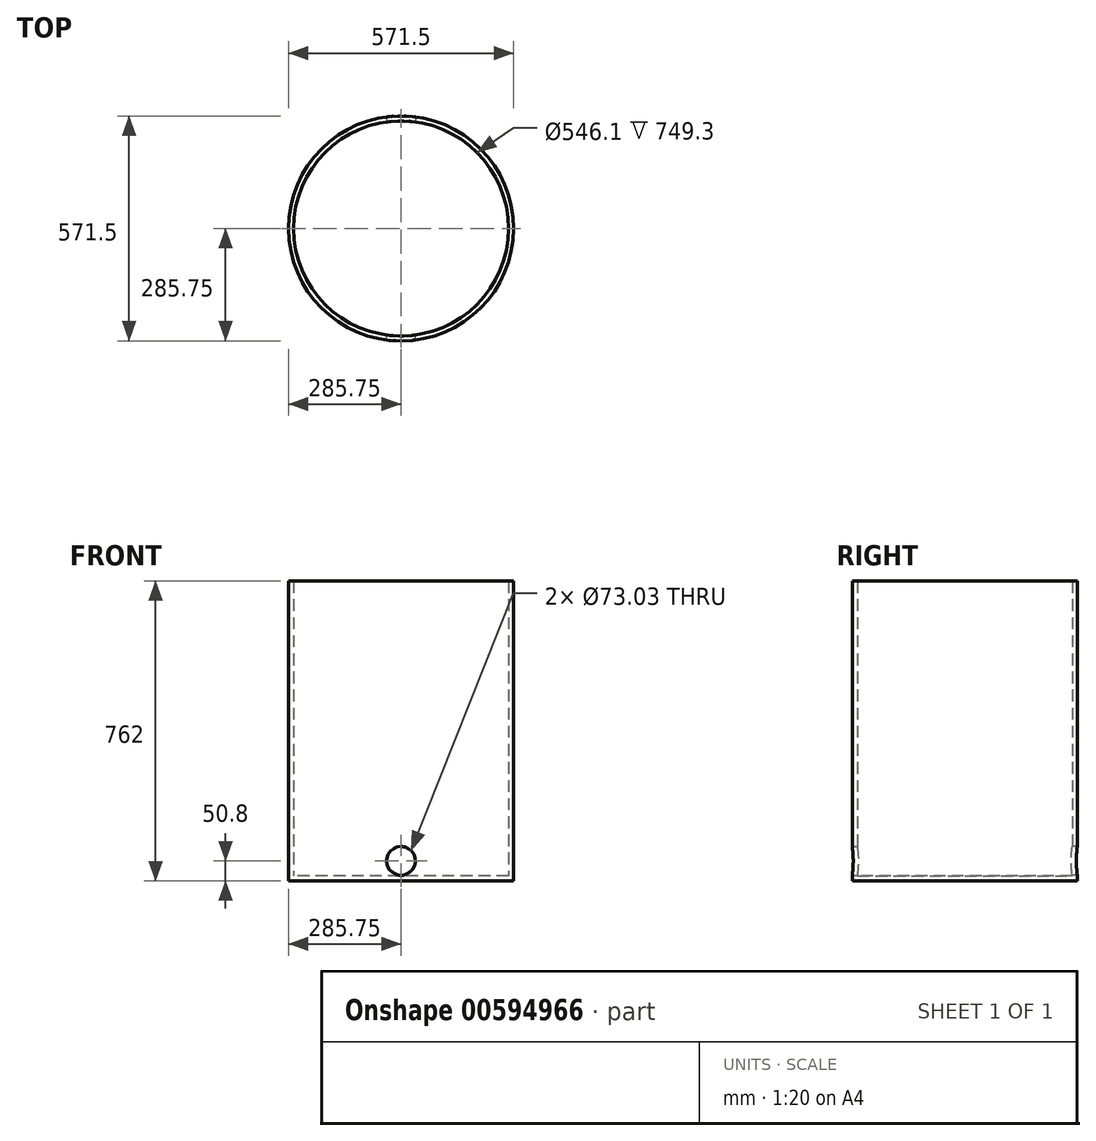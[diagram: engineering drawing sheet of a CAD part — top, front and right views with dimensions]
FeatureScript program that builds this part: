
annotation { "Feature Type Name" : "Feature", "Feature Type Description" : "" }
export const myFeature = defineFeature(function(context is Context, id is Id, definition is map)
    precondition{}
    {
        {
            var Q0;
            Q0=qCreatedBy(makeId("Top.planeOp"),FACE);
            var sketch = newSketch(context, id + "F0", { "sketchPlane" : qUnion([Q0])});
            skCircle(sketch, "E0", {"center": v(0, 0) * mm, "radius": 285.75 * mm});
            skSolve(sketch);
        }
        {
            var Q0;
            Q0=qSketchRegion(id+"F0",true);
            extrude(context, id + "F1", {"entities" : qUnion([Q0]), "depth" : 762 * mm, "offsetDistance" : 25.4 * mm});
        }
        {
            var Q0;
            Q0=makeQuery(id+"F1.opExtrude","CAP_FACE",FACE,{"disambiguationData":[OSD([sQuery(id+"F0.wireOp",EDGE,"E0")])],"isStart":false});
            shell(context, id + "F2", {"entities" : qUnion([Q0]), "thickness" : 12.7 * mm});
        }
        {
            var Q0;
            Q0=qCreatedBy(makeId("Front.planeOp"),FACE);
            var sketch = newSketch(context, id + "F3", { "sketchPlane" : qUnion([Q0])});
            skLineSegment(sketch, "E1", {"start": v(0, 0) * mm, "end": v(0, 101.6) * mm, "construction": true});
            skCircle(sketch, "E2", {"center": v(0, 50.8) * mm, "radius": 36.51 * mm});
            skSolve(sketch);
        }
        {
            var Q0;
            Q0=qSketchRegion(id+"F3",true);
            extrude(context, id + "F4", {"entities" : qUnion([Q0]), "operationType" : NewBodyOperationType.REMOVE, "depth" : 327.66 * mm, "offsetDistance" : 25.4 * mm});
        }
        {
            var Q0;
            Q0=qCreatedBy(makeId("Front.planeOp"),FACE);
            var sketch = newSketch(context, id + "F5", { "sketchPlane" : qUnion([Q0])});
            skLineSegment(sketch, "E3", {"start": v(0, 0) * mm, "end": v(0, 101.6) * mm, "construction": true});
            skCircle(sketch, "E4", {"center": v(0, 50.8) * mm, "radius": 36.51 * mm});
            skSolve(sketch);
        }
        {
            var Q0;
            Q0=qSketchRegion(id+"F5",true);
            extrude(context, id + "F6", {"entities" : qUnion([Q0]), "operationType" : NewBodyOperationType.REMOVE, "oppositeDirection" : true, "depth" : 345.44 * mm, "offsetDistance" : 25.4 * mm});
        }
    });
